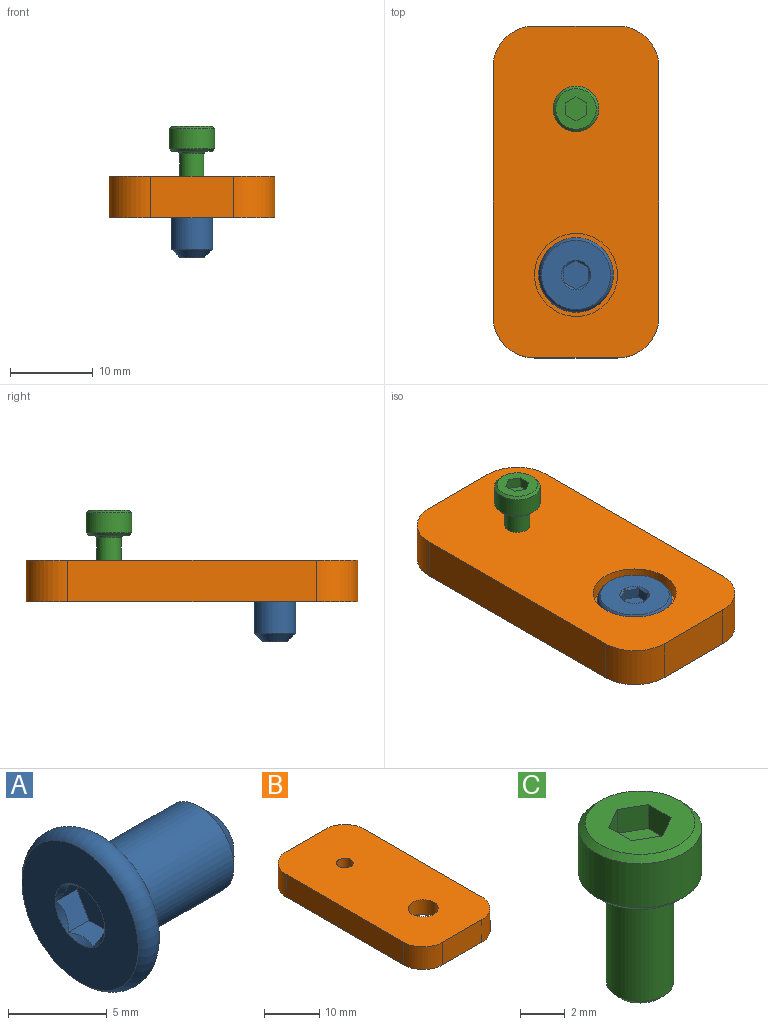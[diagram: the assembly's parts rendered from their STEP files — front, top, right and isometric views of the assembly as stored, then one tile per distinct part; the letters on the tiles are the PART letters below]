
ASSEMBLY  parts=3 mates=2
PART A: 14 faces, bbox 9.8x9.7x9.7 mm
  f0: plane 1.5x1.45mm, normal (0,-0.87,0.5), area 2.2mm2, adj f1,f5,f9,f12
  f1: plane 1.73x1.45mm, normal (0,0,1), area 2.2mm2, adj f0,f2,f9,f12
  f2: plane 1.5x1.45mm, normal (0,0.87,0.5), area 2.2mm2, adj f1,f3,f9,f12
  f3: plane 1.5x1.45mm, normal (0,0.87,-0.5), area 2.2mm2, adj f2,f4,f9,f12
  f4: plane 1.73x1.45mm, normal (0,0,-1), area 2.2mm2, adj f3,f5,f9,f12
  f5: plane 1.5x1.45mm, normal (0,-0.87,-0.5), area 2.2mm2, adj f0,f4,f9,f12
  f6: plane 8.32x8.32mm, normal (-1,0,0), area 44.4mm2, adj f7,f9
  f7: torus R=3.5mm, axis (-1,0,0), area 46.7mm2, adj f6,f8
  f8: plane 8.32x8.32mm, normal (1,0,0), area 34.8mm2, adj f7,f11
  f9: cone r=1.78mm half-angle=45deg, axis (-1,0,0), area 3.1mm2, adj f0,f1,f2,f3,f4,f5,f6
  f10: plane 3x3mm, normal (1,0,0), area 7.1mm2, adj f13
  f11: cylinder r=2.5mm len=7mm, axis (-1,0,0), area 110mm2, adj f8,f13
  f12: plane 3.46x3mm, normal (-1,0,0), area 7.8mm2, adj f0,f1,f2,f3,f4,f5
  f13: cone r=1.5mm half-angle=45deg, axis (-1,0,0), area 17.8mm2, adj f10,f11
PART B: 14 faces, bbox 20x40x5 mm
  f0: plane 10x5mm, normal (0,1,0), area 50mm2, adj f6,f7,f10,f13
  f1: plane 30x5mm, normal (-1,0,0), area 150mm2, adj f6,f7,f10,f11
  f2: plane 10x5mm, normal (0,-1,0), area 50mm2, adj f6,f7,f11,f12
  f3: plane 30x5mm, normal (1,0,0), area 150mm2, adj f6,f7,f12,f13
  f4: cylinder r=1.5mm len=5mm, axis (0,0,-1), area 47.1mm2, adj f6,f7
  f5: cylinder r=2.7mm len=5.4mm, axis (0,0,-1), area 54.3mm2, adj f6,f9
  f6: plane 40x20mm, normal (0,0,1), area 748.6mm2, adj f0,f1,f2,f3,f4,f5,f10,f11
  f7: plane 40x20mm, normal (0,0,-1), area 692.9mm2, adj f0,f1,f2,f3,f4,f8,f10,f11
  f8: cylinder r=5mm len=10mm, axis (0,0,-1), area 56.5mm2, adj f7,f9
  f9: plane 10x10mm, normal (0,0,-1), area 55.6mm2, adj f5,f8
  f10: cylinder r=5mm len=5mm, axis (0,0,-1), area 39.3mm2, adj f0,f1,f6,f7
  f11: cylinder r=5mm len=5mm, axis (0,0,1), area 39.3mm2, adj f1,f2,f6,f7
  f12: cylinder r=5mm len=5mm, axis (0,0,-1), area 39.3mm2, adj f2,f3,f6,f7
  f13: cylinder r=5mm len=5mm, axis (0,0,1), area 39.3mm2, adj f0,f3,f6,f7
PART C: 16 faces, bbox 5.5x5.5x9 mm
  f0: plane 4.9x4.9mm, normal (0,0,1), area 13.4mm2, adj f5,f6,f7,f8,f9,f10,f15
  f1: cylinder r=1.5mm len=5.4mm, axis (0,0,1), area 50.9mm2, adj f12,f14
  f2: plane 2.4x2.4mm, normal (0,0,-1), area 4.5mm2, adj f14
  f3: cylinder r=2.75mm len=5.5mm, axis (0,0,-1), area 41.5mm2, adj f13,f15
  f4: plane 4.9x4.9mm, normal (0,0,-1), area 8.7mm2, adj f12,f13
  f5: plane 1.3x1.25mm, normal (0.5,0.87,0), area 1.9mm2, adj f0,f6,f10,f11
  f6: plane 1.3x1.25mm, normal (-0.5,0.87,0), area 1.9mm2, adj f0,f5,f7,f11
  f7: plane 1.44x1.3mm, normal (-1,0,0), area 1.9mm2, adj f0,f6,f8,f11
  f8: plane 1.3x1.25mm, normal (-0.5,-0.87,0), area 1.9mm2, adj f0,f7,f9,f11
  f9: plane 1.3x1.25mm, normal (0.5,-0.87,0), area 1.9mm2, adj f0,f8,f10,f11
  f10: plane 1.44x1.3mm, normal (1,0,0), area 1.9mm2, adj f0,f5,f9,f11
  f11: plane 2.89x2.5mm, normal (0,0,1), area 5.4mm2, adj f5,f6,f7,f8,f9,f10
  f12: torus R=1.8mm, axis (0,0,1), area 4.8mm2, adj f1,f4
  f13: cone r=2.75mm half-angle=45deg, axis (0,0,1), area 6.9mm2, adj f3,f4
  f14: cone r=1.5mm half-angle=45deg, axis (0,0,1), area 3.6mm2, adj f1,f2
  f15: cone r=2.45mm half-angle=45deg, axis (0,0,-1), area 6.9mm2, adj f0,f3
PLACE A rot(axis=(0.71,0,-0.71),180deg) t=(254.4,-2.23,-95.34)mm
PLACE B rot(axis=(0,-1,0),180deg) t=(414.4,-12.19,-78.54)mm
PLACE C rot(axis=(0,0,1),180deg) t=(254.4,17.77,-75.54)mm
MATE cylindrical C.f3 <-> B.f4  axis (0,0,1) through (254.4,17.77,-78.54)mm
MATE fastened A.f11 <-> B.f5  axis (0,0,-1) through (254.4,-2.23,-80.34)mm
